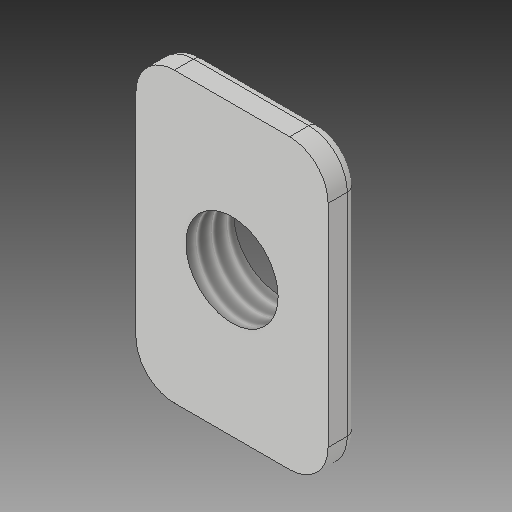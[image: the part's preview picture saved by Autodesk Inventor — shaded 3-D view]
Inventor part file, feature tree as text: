
AUTODESK INVENTOR PART (.ipt)
format: ipt  version: 2017 (Build 210142000, 142)  size: 159,232 bytes
history: native  units: mm
features: other x3, sketch x2
ambient origin geometry x8: Origin, YZ Plane, XZ Plane, XY Plane, X Axis, Y Axis, Z Axis, Center Point
bodies: Solid1 (feature_tree)
feature tree (5):
  other  "M5 Tee Nut-Generic.ipt"
  other  "Solid1::M5 Tee Nut-Generic.ipt"
  other  "TaggingFeature1"
  sketch  "Sketch1"  dims[d0=10.0mm]
  sketch  "Sketch2"
